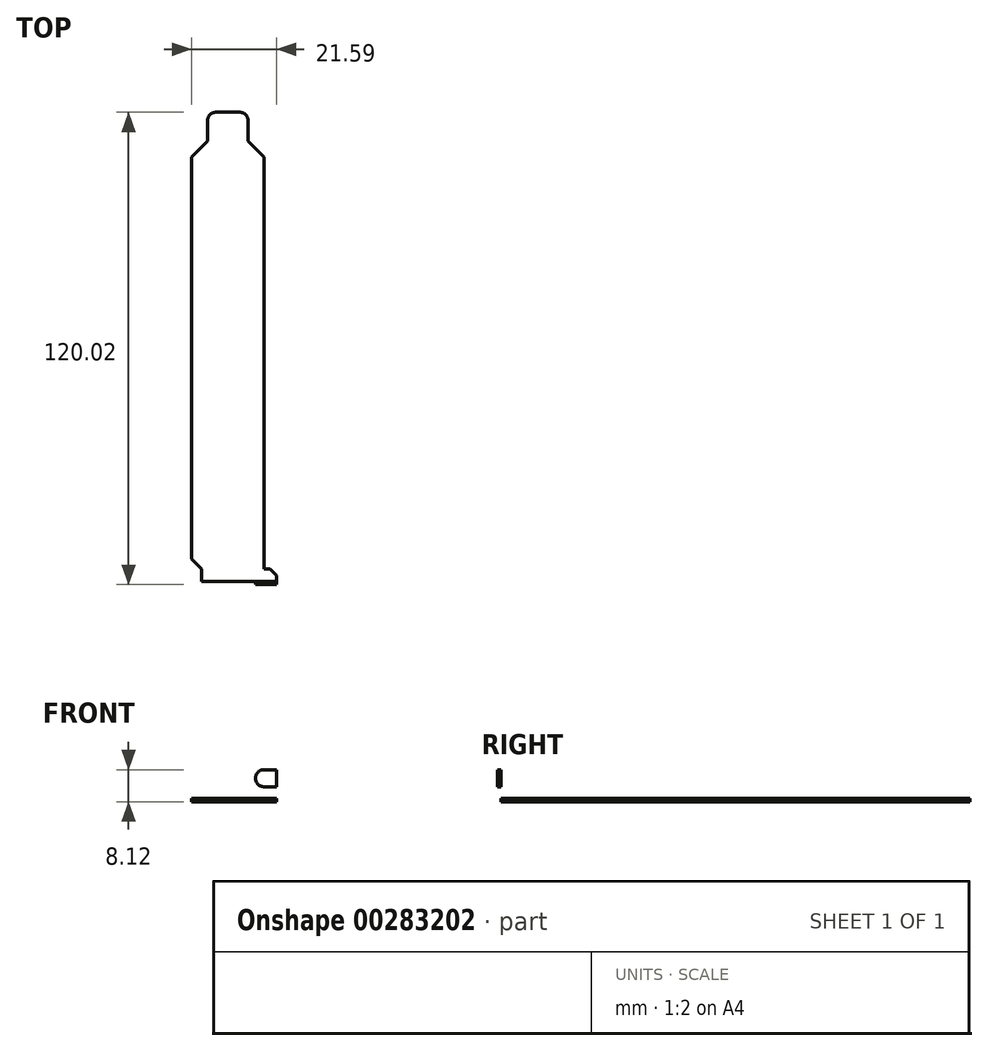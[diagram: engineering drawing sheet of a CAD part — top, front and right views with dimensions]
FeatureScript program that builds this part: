
annotation { "Feature Type Name" : "Feature", "Feature Type Description" : "" }
export const myFeature = defineFeature(function(context is Context, id is Id, definition is map)
    precondition{}
    {
        {
            var Q0;
            Q0=qCreatedBy(makeId("Top.planeOp"),FACE);
            var sketch = newSketch(context, id + "F0", { "sketchPlane" : qUnion([Q0])});
            skPoint(sketch, "E0.middle", {"position": v(0, 0) * mm});
            skPoint(sketch, "E1.0.midPoint", {"position": v(0, -85.82) * mm});
            skLineSegment(sketch, "E2.bottom", {"start": v(3.19, 58.04) * mm, "end": v(-3.19, 58.04) * mm});
            skLineSegment(sketch, "E2.top", {"start": v(9.2, -58.04) * mm, "end": v(-6.67, -58.04) * mm});
            skLineSegment(sketch, "E2.left", {"start": v(9.2, 46.66) * mm, "end": v(9.2, -58.04) * mm});
            skLineSegment(sketch, "E2.right", {"start": v(-9.2, 46.66) * mm, "end": v(-9.2, -55.5) * mm});
            skLineSegment(sketch, "E3.bottom", {"start": v(0, 58.04) * mm, "end": v(3.19, 58.04) * mm});
            skLineSegment(sketch, "E3.right", {"start": v(5.1, 56.13) * mm, "end": v(5.1, 50.77) * mm});
            skLineSegment(sketch, "E4.MirrorCS", {"start": v(-5.1, 56.13) * mm, "end": v(-5.1, 50.77) * mm});
            skLineSegment(sketch, "E5.MirrorCS", {"start": v(0, 58.04) * mm, "end": v(-3.19, 58.04) * mm});
            skLineSegment(sketch, "E6", {"start": v(9.2, 46.66) * mm, "end": v(5.1, 50.77) * mm});
            skLineSegment(sketch, "E7.MirrorCS", {"start": v(-9.2, 46.66) * mm, "end": v(-5.1, 50.77) * mm});
            skPoint(sketch, "E8.MirrorCS.end.orphan", {"position": v(-9.2, 46.66) * mm});
            skArc(sketch, "E9.filletArc", {"start": v(5.1, 56.13) * mm, "mid": v(4.53, 57.48) * mm, "end": v(3.19, 58.04) * mm});
            skArc(sketch, "E10.filletArc", {"start": v(-3.19, 58.04) * mm, "mid": v(-4.53, 57.48) * mm, "end": v(-5.1, 56.13) * mm});
            skLineSegment(sketch, "E11", {"start": v(-6.67, -58.04) * mm, "end": v(-9.2, -55.5) * mm});
            skLineSegment(sketch, "E12.bottom", {"start": v(-6.67, -58.04) * mm, "end": v(10.73, -58.04) * mm});
            skLineSegment(sketch, "E12.top", {"start": v(-6.67, -61.11) * mm, "end": v(12.38, -61.11) * mm});
            skLineSegment(sketch, "E12.left", {"start": v(-6.67, -58.04) * mm, "end": v(-6.67, -61.11) * mm});
            skLineSegment(sketch, "E12.right", {"start": v(12.38, -59.7) * mm, "end": v(12.38, -61.11) * mm});
            skLineSegment(sketch, "E13", {"start": v(10.73, -58.04) * mm, "end": v(12.38, -59.69) * mm});
            skLineSegment(sketch, "E14.top", {"start": v(-6.67, -61.98) * mm, "end": v(12.38, -61.98) * mm});
            skLineSegment(sketch, "E14.left", {"start": v(-6.67, -61.11) * mm, "end": v(-6.67, -61.98) * mm});
            skLineSegment(sketch, "E14.right", {"start": v(12.38, -61.11) * mm, "end": v(12.38, -61.98) * mm});
            skSolve(sketch);
        }
        {
            var Q0;
            {var subQ0=sQuery(id+"F0.wireOp",EDGE,"E12.left");Q0=makeQuery(id+"F0.imprint","IMPRINT",FACE,{"disambiguationData":[TD([[makeQuery(id+"F0.imprint","IMPRINT",EDGE,{"derivedFrom":subQ0}),1.0]])]});}
            var Q1;
            {var subQ0=sQuery(id+"F0.wireOp",EDGE,"E2.left");Q1=makeQuery(id+"F0.imprint","IMPRINT",FACE,{"disambiguationData":[TD([[makeQuery(id+"F0.imprint","IMPRINT",EDGE,{"derivedFrom":subQ0}),-1.0]])]});}
            var Q2;
            Q2 = qSketchRegion(id + "FiseerDxeNEIBDG_2", true);
            extrude(context, id + "F1", {"entities" : qUnion([Q0, Q1, Q2]), "depth" : 0.86 * mm});
        }
        {
            var Q0;
            Q0=makeQuery(id+"F1.opExtrude","SWEPT_FACE",FACE,{"disambiguationData":[OSD([sQuery(id+"F0.wireOp",EDGE,"E12.top")])]});
            extrude(context, id + "F2", {"entities" : qUnion([Q0]), "depth" : 0.86 * mm});
        }
        {
            var Q0;
            {var subQ0=sQuery(id+"F0.wireOp",EDGE,"E12.top");Q0=makeQuery(id+"F2.opExtrude","SWEPT_FACE",FACE,{"disambiguationData":[OSD([subQ0]),TDD([makeQuery(id+"F1.opExtrude","CAP_EDGE",EDGE,{"disambiguationData":[OSD([subQ0])],"isStart":false})])]});}
            extrude(context, id + "F3", {"entities" : qUnion([Q0]), "operationType" : NewBodyOperationType.ADD, "depth" : 11.43 * mm});
        }
        {
            var Q0;
            {var subQ0=sQuery(id+"F0.wireOp",EDGE,"E12.top");Q0=makeQuery(id+"F3.boolean.opBoolean","MERGE",FACE,{"derivedFrom":[makeQuery(id+"F2.opExtrude","CAP_FACE",FACE,{"disambiguationData":[OSD([subQ0])],"isStart":false}),makeQuery(id+"F3.opExtrude","SWEPT_FACE",FACE,{"disambiguationData":[OSD([subQ0]),TDD([makeQuery(id+"F2.opExtrude","CAP_EDGE",EDGE,{"disambiguationData":[OSD([subQ0]),TDD([makeQuery(id+"F1.opExtrude","CAP_EDGE",EDGE,{"disambiguationData":[OSD([subQ0])],"isStart":false})])],"isStart":false})])]})]});}
            var sketch = newSketch(context, id + "F4", { "sketchPlane" : qUnion([Q0])});
            skLineSegment(sketch, "E15", {"start": v(1.71, 12.3) * mm, "end": v(1.71, 8.1) * mm});
            skLineSegment(sketch, "E16", {"start": v(1.71, 8.1) * mm, "end": v(4.76, 8.1) * mm});
            skLineSegment(sketch, "E17", {"start": v(4.76, 8.1) * mm, "end": v(4.76, 12.3) * mm});
            skLineSegment(sketch, "E18", {"start": v(4.76, 8.1) * mm, "end": v(7.18, 12.3) * mm});
            skLineSegment(sketch, "E19", {"start": v(-0.7, 12.3) * mm, "end": v(1.71, 8.1) * mm});
            skLineSegment(sketch, "E20", {"start": v(-0.7, 12.3) * mm, "end": v(1.71, 12.3) * mm});
            skLineSegment(sketch, "E21", {"start": v(4.76, 12.3) * mm, "end": v(7.18, 12.3) * mm});
            skLineSegment(sketch, "E22", {"start": v(-6.67, 10.39) * mm, "end": v(-6.67, 0) * mm});
            skLineSegment(sketch, "E23", {"start": v(-6.67, 0) * mm, "end": v(12.38, 0) * mm});
            skLineSegment(sketch, "E24", {"start": v(12.38, 0) * mm, "end": v(12.38, 10.39) * mm});
            skLineSegment(sketch, "E25", {"start": v(10.48, 12.3) * mm, "end": v(-4.76, 12.3) * mm});
            skPoint(sketch, "E26.visualSharp", {"position": v(-6.67, 12.3) * mm});
            skArc(sketch, "E26.filletArc", {"start": v(-4.76, 12.3) * mm, "mid": v(-6.1, 11.74) * mm, "end": v(-6.67, 10.39) * mm});
            skPoint(sketch, "E27.visualSharp", {"position": v(12.38, 12.3) * mm});
            skArc(sketch, "E27.filletArc", {"start": v(12.38, 10.39) * mm, "mid": v(11.82, 11.74) * mm, "end": v(10.48, 12.3) * mm});
            skLineSegment(sketch, "E28", {"start": v(12.38, 12.3) * mm, "end": v(12.38, 0) * mm});
            skArc(sketch, "E29", {"start": v(7.03, 5.94) * mm, "mid": v(7.67, 7.49) * mm, "end": v(9.2, 8.12) * mm});
            skArc(sketch, "E30.MirrorCS", {"start": v(7.03, 5.94) * mm, "mid": v(7.67, 4.4) * mm, "end": v(9.2, 3.76) * mm});
            skLineSegment(sketch, "E31", {"start": v(9.2, 8.12) * mm, "end": v(12.38, 8.12) * mm});
            skLineSegment(sketch, "E32", {"start": v(9.2, 3.76) * mm, "end": v(12.38, 3.76) * mm});
            skSolve(sketch);
        }
        {
            var Q0;
            Q0=makeQuery(id+"F4.imprint","IMPRINT",FACE,{"disambiguationData":[TD([[makeQuery(id+"F4.imprint","IMPRINT",EDGE,{"derivedFrom":sQuery(id+"F4.wireOp",EDGE,"E29")}),-1.0]])]});
            var Q1;
            {var subQ0=sQuery(id+"F4.wireOp",EDGE,"E15");Q1=makeQuery(id+"F4.imprint","IMPRINT",FACE,{"disambiguationData":[TD([[makeQuery(id+"F4.imprint","IMPRINT",EDGE,{"derivedFrom":subQ0}),-1.0]])]});}
            var Q2;
            {var subQ0=sQuery(id+"F4.wireOp",EDGE,"E15");Q2=makeQuery(id+"F4.imprint","IMPRINT",FACE,{"disambiguationData":[TD([[makeQuery(id+"F4.imprint","IMPRINT",EDGE,{"derivedFrom":subQ0}),1.0]])]});}
            var Q3;
            {var subQ0=sQuery(id+"F4.wireOp",EDGE,"E17");Q3=makeQuery(id+"F4.imprint","IMPRINT",FACE,{"disambiguationData":[TD([[makeQuery(id+"F4.imprint","IMPRINT",EDGE,{"derivedFrom":subQ0}),-1.0]])]});}
            var Q4;
            {var subQ0=sQuery(id+"F4.wireOp",EDGE,"E27.filletArc");Q4=makeQuery(id+"F4.imprint","IMPRINT",FACE,{"disambiguationData":[TD([[makeQuery(id+"F4.imprint","IMPRINT",EDGE,{"derivedFrom":subQ0}),-1.0]])]});}
            var Q5;
            {var subQ0=sQuery(id+"F4.wireOp",EDGE,"E26.filletArc");Q5=makeQuery(id+"F4.imprint","IMPRINT",FACE,{"disambiguationData":[TD([[makeQuery(id+"F4.imprint","IMPRINT",EDGE,{"derivedFrom":subQ0}),-1.0]])]});}
            extrude(context, id + "F5", {"entities" : qUnion([Q0, Q1, Q2, Q3, Q4, Q5]), "operationType" : NewBodyOperationType.REMOVE, "oppositeDirection" : true, "depth" : 0.86 * mm});
        }
    });
